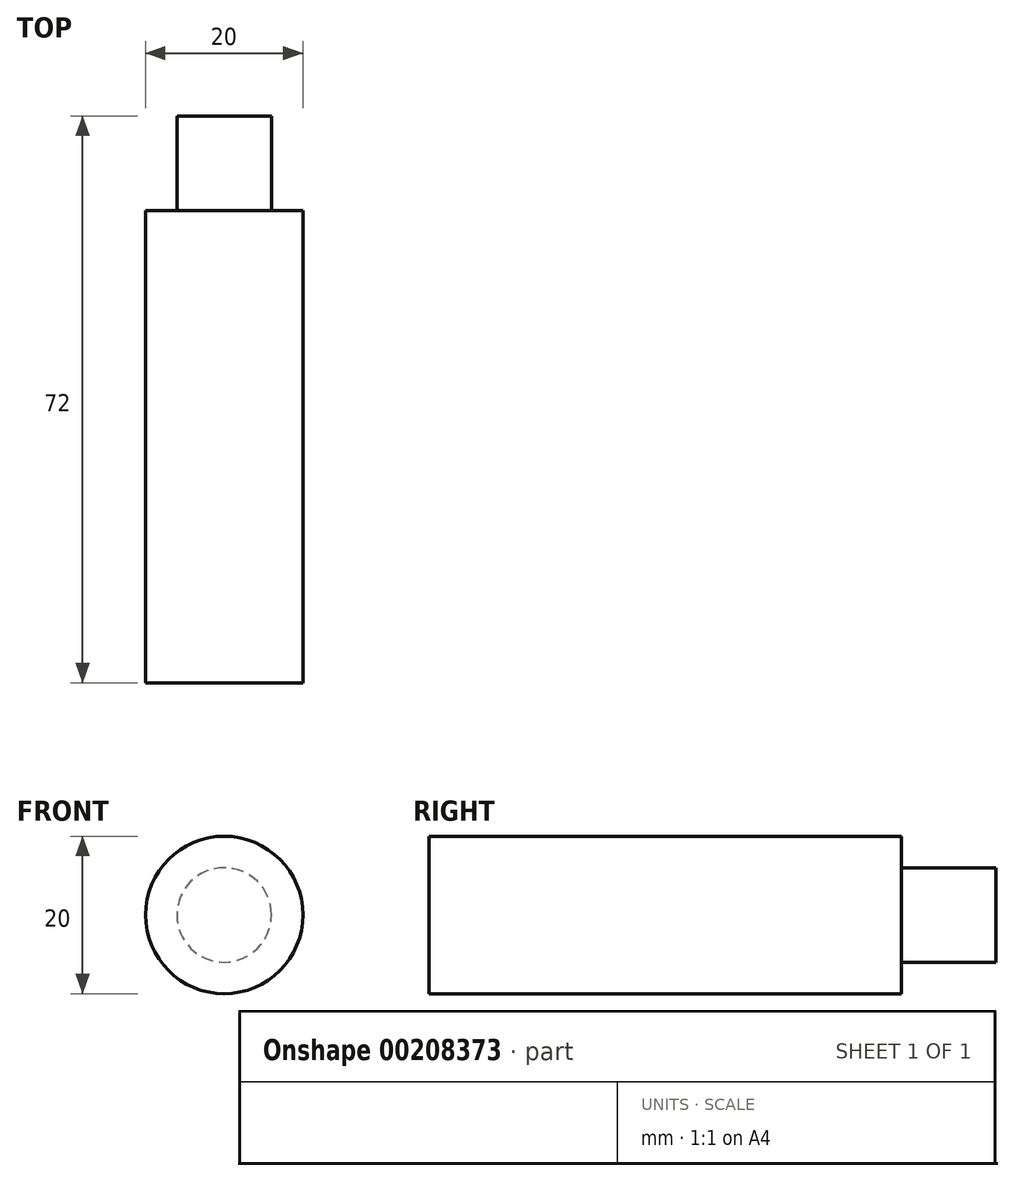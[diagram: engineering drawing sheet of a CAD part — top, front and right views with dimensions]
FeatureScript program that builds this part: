
annotation { "Feature Type Name" : "Feature", "Feature Type Description" : "" }
export const myFeature = defineFeature(function(context is Context, id is Id, definition is map)
    precondition{}
    {
        {
            var Q0;
            Q0=qCreatedBy(makeId("Front.planeOp"),FACE);
            var sketch = newSketch(context, id + "F0", { "sketchPlane" : qUnion([Q0])});
            skCircle(sketch, "E0", {"center": v(0, 0) * mm, "radius": 10 * mm});
            skSolve(sketch);
        }
        {
            var Q0;
            Q0 = qSketchRegion(id + "F0", true);
            extrude(context, id + "F2", {"entities" : qUnion([Q0]), "depth" : 60 * mm});
        }
        {
            var Q0;
            Q0=qCreatedBy(makeId("Front.planeOp"),FACE);
            var sketch = newSketch(context, id + "F3", { "sketchPlane" : qUnion([Q0])});
            skCircle(sketch, "E1", {"center": v(0, 0) * mm, "radius": 6 * mm});
            skSolve(sketch);
        }
        {
            var Q0;
            Q0 = qSketchRegion(id + "F3", true);
            extrude(context, id + "F1", {"entities" : qUnion([Q0]), "operationType" : NewBodyOperationType.ADD, "oppositeDirection" : true, "depth" : 12 * mm});
        }
    });
